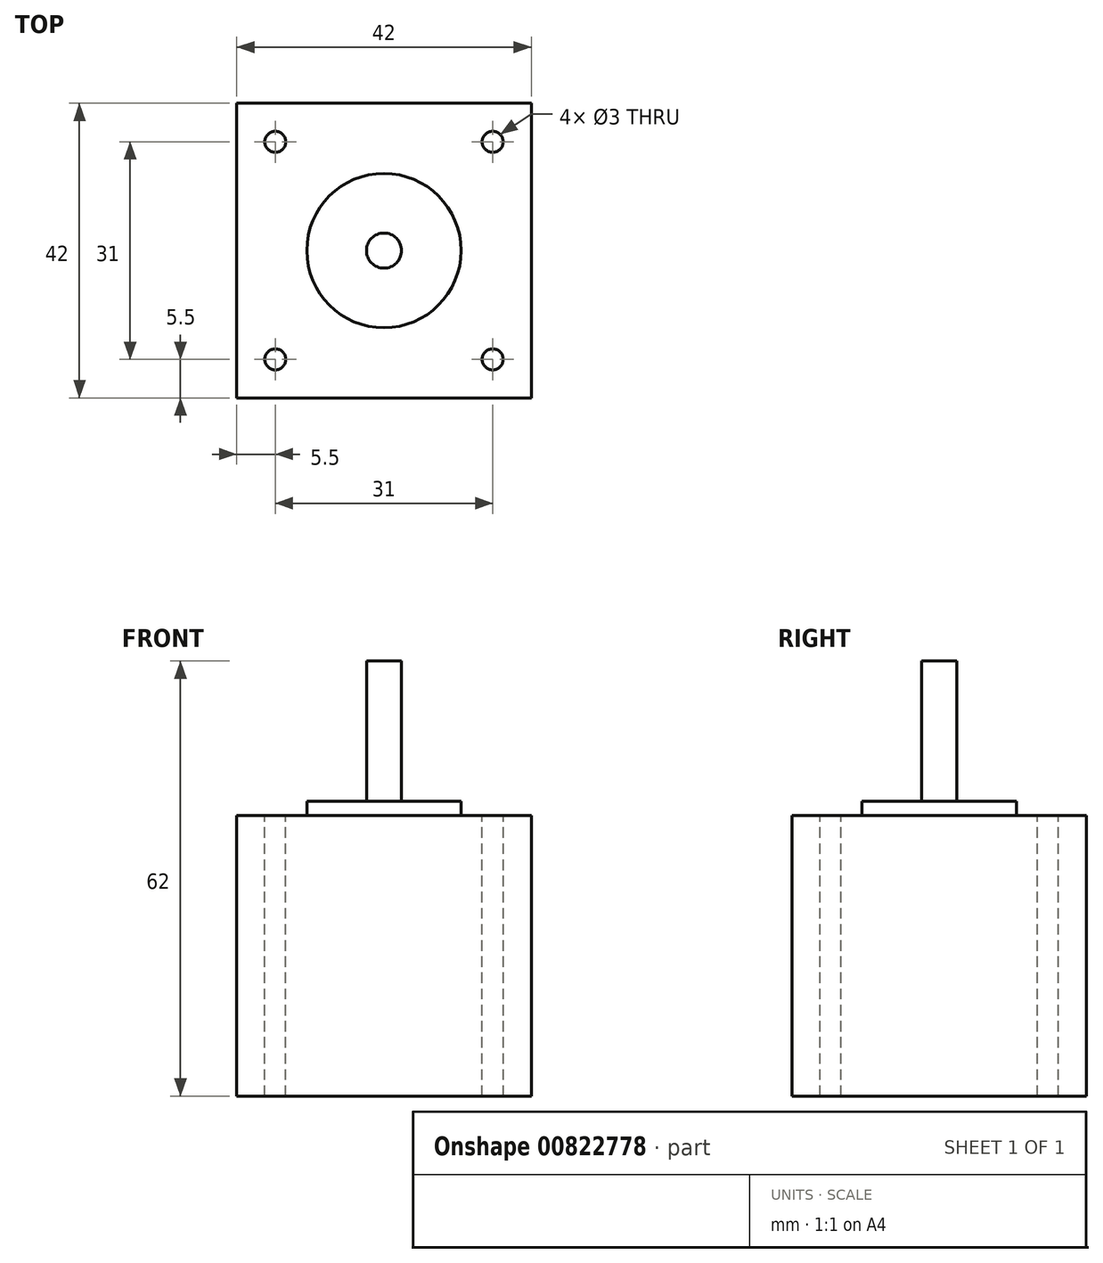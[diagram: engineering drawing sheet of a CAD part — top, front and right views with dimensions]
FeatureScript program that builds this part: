
annotation { "Feature Type Name" : "Feature", "Feature Type Description" : "" }
export const myFeature = defineFeature(function(context is Context, id is Id, definition is map)
    precondition{}
    {
        {
            var Q0;
            Q0=qCreatedBy(makeId("Top.planeOp"),FACE);
            var sketch = newSketch(context, id + "F0", { "sketchPlane" : qUnion([Q0])});
            skLineSegment(sketch, "E0.bottom", {"start": v(-21, 21) * mm, "end": v(21, 21) * mm});
            skLineSegment(sketch, "E0.top", {"start": v(-21, -21) * mm, "end": v(21, -21) * mm});
            skLineSegment(sketch, "E0.left", {"start": v(-21, 21) * mm, "end": v(-21, -21) * mm});
            skLineSegment(sketch, "E0.right", {"start": v(21, 21) * mm, "end": v(21, -21) * mm});
            skCircle(sketch, "E1", {"center": v(0, 0) * mm, "radius": 21 * mm, "construction": true});
            skLineSegment(sketch, "E2.bottom", {"start": v(15.5, -15.5) * mm, "end": v(-15.5, -15.5) * mm, "construction": true});
            skLineSegment(sketch, "E2.top", {"start": v(15.5, 15.5) * mm, "end": v(-15.5, 15.5) * mm, "construction": true});
            skLineSegment(sketch, "E2.left", {"start": v(15.5, -15.5) * mm, "end": v(15.5, 15.5) * mm, "construction": true});
            skLineSegment(sketch, "E2.right", {"start": v(-15.5, -15.5) * mm, "end": v(-15.5, 15.5) * mm, "construction": true});
            skCircle(sketch, "E3", {"center": v(-15.5, 15.5) * mm, "radius": 1.5 * mm, "construction": true});
            skCircle(sketch, "E4", {"center": v(15.5, 15.5) * mm, "radius": 1.5 * mm, "construction": true});
            skCircle(sketch, "E5", {"center": v(15.5, -15.5) * mm, "radius": 1.5 * mm, "construction": true});
            skCircle(sketch, "E6", {"center": v(-15.5, -15.5) * mm, "radius": 1.5 * mm, "construction": true});
            skCircle(sketch, "E7", {"center": v(0, 0) * mm, "radius": 11 * mm});
            skSolve(sketch);
        }
        {
            var Q0;
            Q0=makeQuery(id+"F0.imprint","IMPRINT",FACE,{"disambiguationData":[TD([[makeQuery(id+"F0.imprint","IMPRINT",EDGE,{"derivedFrom":sQuery(id+"F0.wireOp",EDGE,"E0.bottom")}),-1.0]])]});
            var Q1;
            Q1=makeQuery(id+"F0.imprint","IMPRINT",FACE,{"disambiguationData":[TD([[makeQuery(id+"F0.imprint","IMPRINT",EDGE,{"derivedFrom":sQuery(id+"F0.wireOp",EDGE,"E7")}),1.0]])]});
            extrude(context, id + "F1", {"entities" : qUnion([Q0, Q1]), "depth" : 40 * mm, "offsetDistance" : 25 * mm});
        }
        {
            var Q0;
            Q0=makeQuery(id+"F1.opExtrude","CAP_FACE",FACE,{"disambiguationData":[OSD([sQuery(id+"F0.wireOp",EDGE,"E0.bottom"),sQuery(id+"F0.wireOp",EDGE,"E0.top"),sQuery(id+"F0.wireOp",EDGE,"E0.left"),sQuery(id+"F0.wireOp",EDGE,"E0.right"),sQuery(id+"F0.wireOp",EDGE,"E3"),sQuery(id+"F0.wireOp",EDGE,"E4"),sQuery(id+"F0.wireOp",EDGE,"E5"),sQuery(id+"F0.wireOp",EDGE,"E6")])],"isStart":false});
            var sketch = newSketch(context, id + "F2", { "sketchPlane" : qUnion([Q0])});
            skCircle(sketch, "E8.0", {"center": v(0, 0) * mm, "radius": 11 * mm});
            skSolve(sketch);
        }
        {
            var Q0;
            Q0=makeQuery(id+"F2.imprint","IMPRINT",FACE,{"disambiguationData":[TD([[makeQuery(id+"F2.imprint","IMPRINT",EDGE,{"derivedFrom":sQuery(id+"F2.wireOp",EDGE,"E8.0")}),1.0]])]});
            extrude(context, id + "F3", {"entities" : qUnion([Q0]), "operationType" : NewBodyOperationType.ADD, "depth" : 2 * mm, "offsetDistance" : 25 * mm});
        }
        {
            var Q0;
            Q0=makeQuery(id+"F3.opExtrude","CAP_FACE",FACE,{"disambiguationData":[OSD([sQuery(id+"F2.wireOp",EDGE,"E8.0")])],"isStart":false});
            var sketch = newSketch(context, id + "F4", { "sketchPlane" : qUnion([Q0])});
            skPoint(sketch, "E9.0", {"position": v(0, 0) * mm});
            skCircle(sketch, "E10", {"center": v(0, 0) * mm, "radius": 2.5 * mm});
            skSolve(sketch);
        }
        {
            var Q0;
            Q0=makeQuery(id+"F4.imprint","IMPRINT",FACE,{"disambiguationData":[TD([[makeQuery(id+"F4.imprint","IMPRINT",EDGE,{"derivedFrom":sQuery(id+"F4.wireOp",EDGE,"E10")}),1.0]])]});
            extrude(context, id + "F5", {"entities" : qUnion([Q0]), "operationType" : NewBodyOperationType.ADD, "depth" : 20 * mm, "offsetDistance" : 25 * mm});
        }
        {
            var Q0;
            Q0=makeQuery(id+"F1.opExtrude","CAP_FACE",FACE,{"disambiguationData":[OSD([sQuery(id+"F0.wireOp",EDGE,"E0.bottom"),sQuery(id+"F0.wireOp",EDGE,"E0.top"),sQuery(id+"F0.wireOp",EDGE,"E0.left"),sQuery(id+"F0.wireOp",EDGE,"E0.right")])],"isStart":false});
            var sketch = newSketch(context, id + "F6", { "sketchPlane" : qUnion([Q0])});
            skCircle(sketch, "E11.0", {"center": v(-15.5, 15.5) * mm, "radius": 1.5 * mm});
            skCircle(sketch, "E11.1", {"center": v(15.5, 15.5) * mm, "radius": 1.5 * mm});
            skCircle(sketch, "E11.2", {"center": v(15.5, -15.5) * mm, "radius": 1.5 * mm});
            skCircle(sketch, "E11.3", {"center": v(-15.5, -15.5) * mm, "radius": 1.5 * mm});
            skSolve(sketch);
        }
        {
            var Q0;
            Q0=makeQuery(id+"F6.imprint","IMPRINT",FACE,{"disambiguationData":[TD([[makeQuery(id+"F6.imprint","IMPRINT",EDGE,{"derivedFrom":sQuery(id+"F6.wireOp",EDGE,"E11.0")}),1.0]])]});
            var Q1;
            Q1=makeQuery(id+"F6.imprint","IMPRINT",FACE,{"disambiguationData":[TD([[makeQuery(id+"F6.imprint","IMPRINT",EDGE,{"derivedFrom":sQuery(id+"F6.wireOp",EDGE,"E11.1")}),1.0]])]});
            var Q2;
            Q2=makeQuery(id+"F6.imprint","IMPRINT",FACE,{"disambiguationData":[TD([[makeQuery(id+"F6.imprint","IMPRINT",EDGE,{"derivedFrom":sQuery(id+"F6.wireOp",EDGE,"E11.2")}),1.0]])]});
            var Q3;
            Q3=makeQuery(id+"F6.imprint","IMPRINT",FACE,{"disambiguationData":[TD([[makeQuery(id+"F6.imprint","IMPRINT",EDGE,{"derivedFrom":sQuery(id+"F6.wireOp",EDGE,"E11.3")}),1.0]])]});
            var Q4;
            Q4=sQuery(id+"F6.wireOp",EDGE,"E11.0");
            var Q5;
            Q5=sQuery(id+"F6.wireOp",EDGE,"E11.1");
            var Q6;
            Q6=sQuery(id+"F6.wireOp",EDGE,"E11.2");
            var Q7;
            Q7=sQuery(id+"F6.wireOp",EDGE,"E11.3");
            extrude(context, id + "F7", {"entities" : qUnion([Q0, Q1, Q2, Q3]), "operationType" : NewBodyOperationType.REMOVE, "surfaceEntities" : qUnion([Q4, Q5, Q6, Q7]), "endBound" : BoundingType.THROUGH_ALL, "oppositeDirection" : true, "depth" : 25 * mm, "offsetDistance" : 25 * mm});
        }
    });
